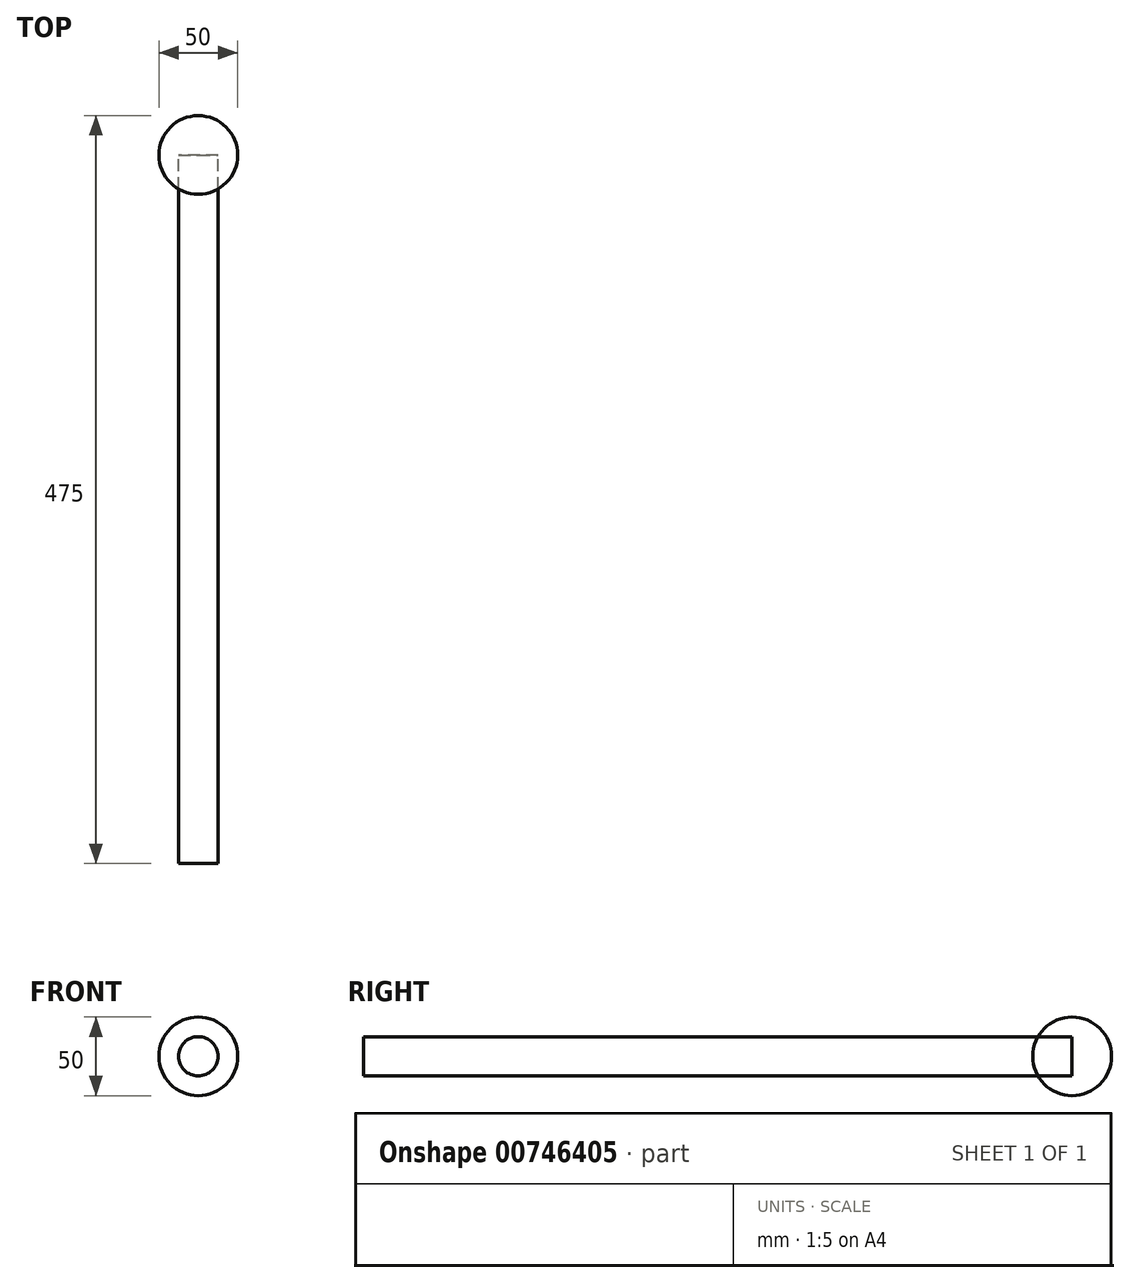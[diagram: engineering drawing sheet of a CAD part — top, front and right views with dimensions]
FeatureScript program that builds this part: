
annotation { "Feature Type Name" : "Feature", "Feature Type Description" : "" }
export const myFeature = defineFeature(function(context is Context, id is Id, definition is map)
    precondition{}
    {
        {
            var Q0;
            Q0=qCreatedBy(makeId("Front.planeOp"),FACE);
            var sketch = newSketch(context, id + "F0", { "sketchPlane" : qUnion([Q0])});
            skArc(sketch, "E0", {"start": v(0, -25) * mm, "mid": v(25, 0) * mm, "end": v(0, 25) * mm});
            skLineSegment(sketch, "E1", {"start": v(0, 25) * mm, "end": v(0, -25) * mm});
            skSolve(sketch);
        }
        {
            var Q0;
            Q0=makeQuery(id+"F0.imprint","IMPRINT",FACE,{"disambiguationData":[TD([[makeQuery(id+"F0.imprint","IMPRINT",EDGE,{"derivedFrom":sQuery(id+"F0.wireOp",EDGE,"E0")}),1.0]])]});
            var Q1;
            Q1=sQuery(id+"F0.wireOp",EDGE,"E1");
            revolve(context, id + "F1", {"entities" : qUnion([Q0]), "axis" : qUnion([Q1]), "revolveType" : RevolveType.FULL});
        }
        {
            var Q0;
            Q0=qCreatedBy(makeId("Front.planeOp"),FACE);
            var sketch = newSketch(context, id + "F2", { "sketchPlane" : qUnion([Q0])});
            skCircle(sketch, "E2", {"center": v(0, 0) * mm, "radius": 12.5 * mm});
            skSolve(sketch);
        }
        {
            var Q0;
            Q0=makeQuery(id+"F2.imprint","IMPRINT",FACE,{"disambiguationData":[TD([[makeQuery(id+"F2.imprint","IMPRINT",EDGE,{"derivedFrom":sQuery(id+"F2.wireOp",EDGE,"E2")}),1.0]])]});
            extrude(context, id + "F3", {"entities" : qUnion([Q0]), "depth" : 450 * mm, "offsetDistance" : 25 * mm});
        }
    });
